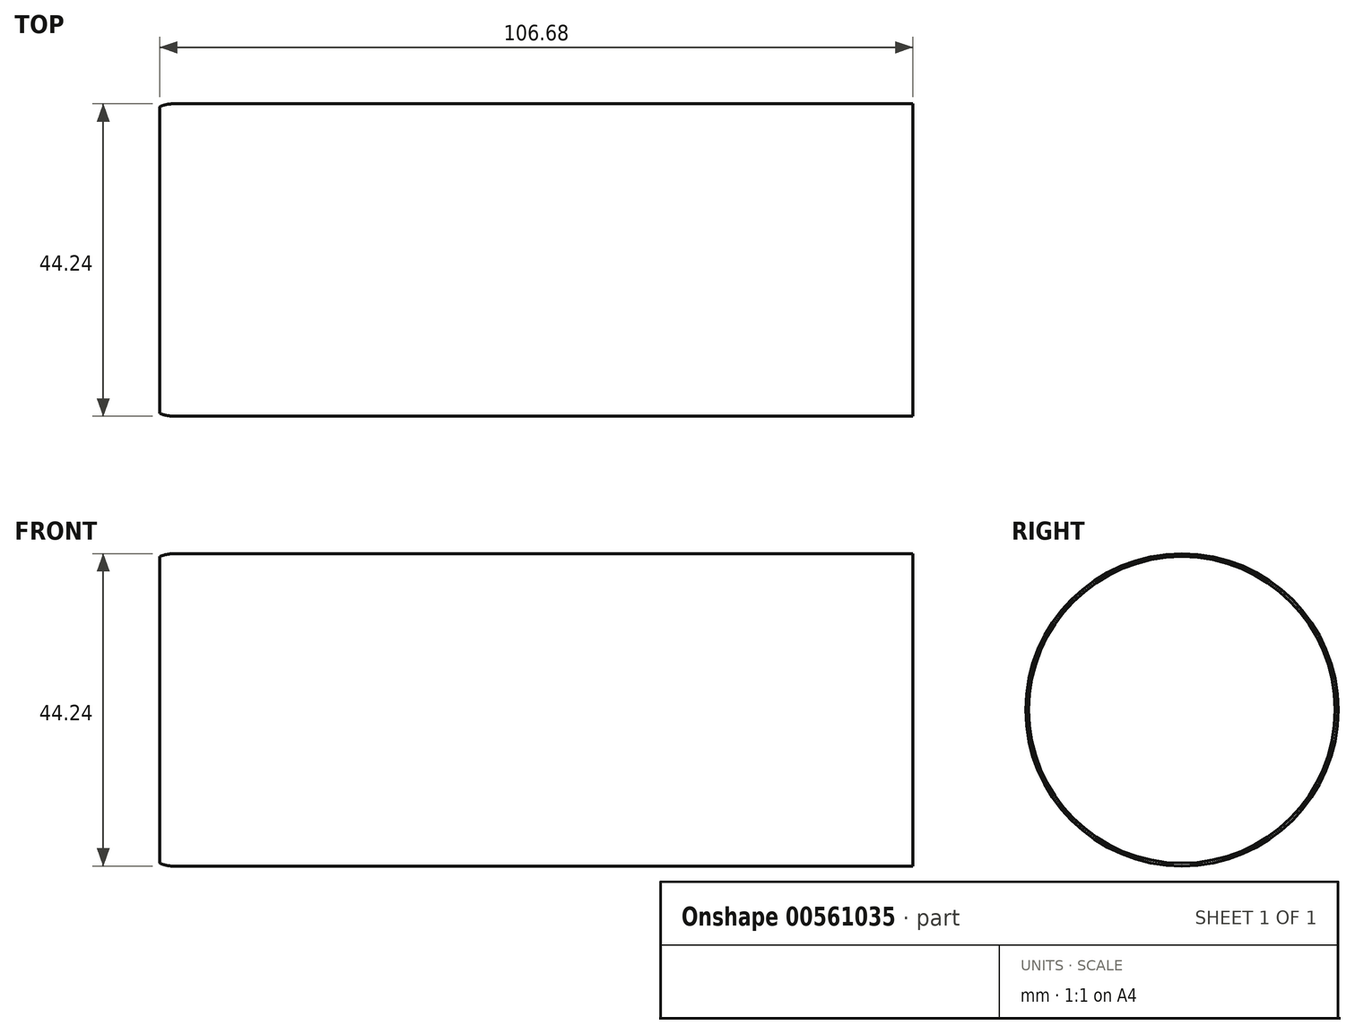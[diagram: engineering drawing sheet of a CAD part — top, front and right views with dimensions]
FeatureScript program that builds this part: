
annotation { "Feature Type Name" : "Feature", "Feature Type Description" : "" }
export const myFeature = defineFeature(function(context is Context, id is Id, definition is map)
    precondition{}
    {
        {
            var Q0;
            Q0=qCreatedBy(makeId("Top.planeOp"),FACE);
            var sketch = newSketch(context, id + "F0", { "sketchPlane" : qUnion([Q0])});
            skLineSegment(sketch, "E0.bottom", {"start": v(-51.03, 22.12) * mm, "end": v(53.67, 22.12) * mm});
            skLineSegment(sketch, "E0.top", {"start": v(-51.33, -22.12) * mm, "end": v(58.38, -22.12) * mm});
            skLineSegment(sketch, "E0.left", {"start": v(-52.06, 22.12) * mm, "end": v(-52.06, -22.12) * mm});
            skLineSegment(sketch, "E0.right", {"start": v(53.67, 22.12) * mm, "end": v(53.67, -22.12) * mm});
            skLineSegment(sketch, "E1", {"start": v(-53, 21.72) * mm, "end": v(-74.44, 12.48) * mm});
            skLineSegment(sketch, "E2", {"start": v(-76.57, 10.74) * mm, "end": v(-79.04, 7.18) * mm});
            skLineSegment(sketch, "E3", {"start": v(-79.04, 7.18) * mm, "end": v(-86.12, 2.68) * mm});
            skLineSegment(sketch, "E4", {"start": v(-87.66, -4.22) * mm, "end": v(-86.92, -5.4) * mm});
            skLineSegment(sketch, "E5", {"start": v(-85.42, -6.9) * mm, "end": v(-71.16, -16.2) * mm});
            skLineSegment(sketch, "E6", {"start": v(-69.86, -16.8) * mm, "end": v(-52.76, -21.91) * mm});
            skPoint(sketch, "E7.visualSharp", {"position": v(-75.76, 11.91) * mm});
            skArc(sketch, "E7.filletArc", {"start": v(-74.44, 12.48) * mm, "mid": v(-75.47, 11.88) * mm, "end": v(-76.33, 11.06) * mm});
            skPoint(sketch, "E8.visualSharp", {"position": v(-76.57, 10.74) * mm});
            skArc(sketch, "E8.filletArc", {"start": v(-76.33, 11.06) * mm, "mid": v(-76.46, 10.9) * mm, "end": v(-76.57, 10.74) * mm});
            skArc(sketch, "E9.filletArc", {"start": v(-86.12, 2.68) * mm, "mid": v(-88.32, -0.45) * mm, "end": v(-87.66, -4.22) * mm});
            skPoint(sketch, "E10.visualSharp", {"position": v(-86.33, -6.31) * mm});
            skArc(sketch, "E10.filletArc", {"start": v(-86.92, -5.4) * mm, "mid": v(-86.25, -6.23) * mm, "end": v(-85.42, -6.9) * mm});
            skPoint(sketch, "E11.visualSharp", {"position": v(-52.06, 22.12) * mm});
            skArc(sketch, "E11.filletArc", {"start": v(-51.03, 22.12) * mm, "mid": v(-52.04, 22.02) * mm, "end": v(-53, 21.72) * mm});
            skPoint(sketch, "E12.visualSharp", {"position": v(-70.55, -16.59) * mm});
            skArc(sketch, "E12.filletArc", {"start": v(-71.16, -16.2) * mm, "mid": v(-70.53, -16.54) * mm, "end": v(-69.86, -16.8) * mm});
            skPoint(sketch, "E13.visualSharp", {"position": v(-52.06, -22.12) * mm});
            skArc(sketch, "E13.filletArc", {"start": v(-52.76, -21.91) * mm, "mid": v(-52.05, -22.07) * mm, "end": v(-51.33, -22.12) * mm});
            skPoint(sketch, "E14.endSnap0", {"position": v(53.67, 0) * mm});
            skLineSegment(sketch, "E15", {"start": v(141.36, 22.76) * mm, "end": v(53.67, 22.12) * mm});
            skPoint(sketch, "E16.visualSharp", {"position": v(53.67, -22.12) * mm});
            skArc(sketch, "E16.filletArc", {"start": v(58.38, -22.12) * mm, "mid": v(60.8, -21.98) * mm, "end": v(63.17, -21.54) * mm});
            skLineSegment(sketch, "E17", {"start": v(63.17, -21.54) * mm, "end": v(87.81, -18.49) * mm});
            skLineSegment(sketch, "E18", {"start": v(95.48, -15.89) * mm, "end": v(126.67, 2.43) * mm});
            skLineSegment(sketch, "E19", {"start": v(133.9, 9.74) * mm, "end": v(141.36, 22.76) * mm});
            skPoint(sketch, "E20.visualSharp", {"position": v(131.26, 5.12) * mm});
            skArc(sketch, "E20.filletArc", {"start": v(126.67, 2.43) * mm, "mid": v(130.76, 5.61) * mm, "end": v(133.9, 9.74) * mm});
            skPoint(sketch, "E21.visualSharp", {"position": v(91.92, -17.98) * mm});
            skArc(sketch, "E21.filletArc", {"start": v(87.81, -18.49) * mm, "mid": v(91.78, -17.58) * mm, "end": v(95.48, -15.89) * mm});
            skLineSegment(sketch, "E22", {"start": v(-52.06, 0) * mm, "end": v(-88.2, 0) * mm, "construction": true});
            skSolve(sketch);
        }
        {
            var Q0;
            Q0=sQuery(id+"F0.wireOp",EDGE,"E22");
            var Q1;
            Q1=sQuery(id+"F0.wireOp",EDGE,"E0.bottom");
            var Q2;
            Q2=sQuery(id+"F0.wireOp",EDGE,"E11.filletArc");
            var Q3;
            Q3=sQuery(id+"F0.wireOp",EDGE,"E22");
            revolve(context, id + "F1", {"bodyType" : ToolBodyType.SURFACE, "surfaceEntities" : qUnion([Q0, Q1, Q2]), "axis" : qUnion([Q3]), "revolveType" : RevolveType.FULL});
        }
    });
